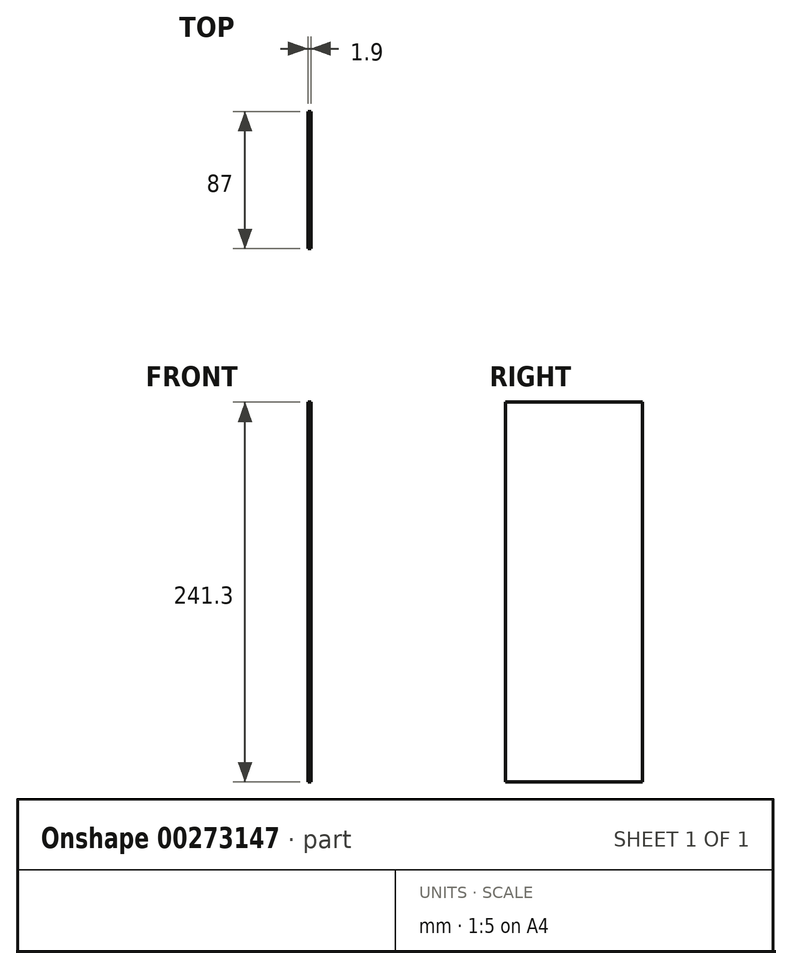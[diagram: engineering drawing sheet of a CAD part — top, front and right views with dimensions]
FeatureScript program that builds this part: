
annotation { "Feature Type Name" : "Feature", "Feature Type Description" : "" }
export const myFeature = defineFeature(function(context is Context, id is Id, definition is map)
    precondition{}
    {
        {
            var Q0;
            Q0=qCreatedBy(makeId("Right.planeOp"),FACE);
            var sketch = newSketch(context, id + "F0", { "sketchPlane" : qUnion([Q0])});
            skLineSegment(sketch, "E0.bottom", {"start": v(0, 0) * mm, "end": v(-87, 0) * mm});
            skLineSegment(sketch, "E0.top", {"start": v(0, -241.3) * mm, "end": v(-87, -241.3) * mm});
            skLineSegment(sketch, "E0.left", {"start": v(0, 0) * mm, "end": v(0, -241.3) * mm});
            skLineSegment(sketch, "E0.right", {"start": v(-87, 0) * mm, "end": v(-87, -241.3) * mm});
            skSolve(sketch);
        }
        {
            var Q0;
            Q0 = qSketchRegion(id + "F0", true);
            extrude(context, id + "F1", {"entities" : qUnion([Q0]), "depth" : 1.9 * mm});
        }
    });
